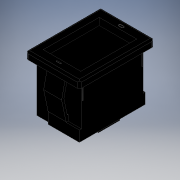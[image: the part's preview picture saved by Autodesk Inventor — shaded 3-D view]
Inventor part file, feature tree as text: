
AUTODESK INVENTOR PART (.ipt)
format: ipt  version: 2019 (Build 230136000, 136)  size: 359,936 bytes
history: native  units: in
note: dims shown in document units (in); Inventor stores cm internally (conversion verified against a paired STEP export)
features: other x21, extrude x11, sketch x11
ambient origin geometry x8: Origin, YZ Plane, XZ Plane, XY Plane, X Axis, Y Axis, Z Axis, Center Point
bodies: Solid1 (feature_tree)
feature tree (43):
  extrude  "Extrusion1"  Depth=0.079in TaperAngle=0.0deg
  extrude  "Extrusion2"  Depth=0.598in TaperAngle=0.0deg
  extrude  "Extrusion3"  Depth=0.2in TaperAngle=0.0deg
  extrude  "Extrusion4"  Depth=0.082in TaperAngle=0.0deg
  extrude  "Extrusion5"  Depth=0.039in TaperAngle=0.0deg
  extrude  "Extrusion6"  TaperAngle=0.0deg  [1 undecoded]
  extrude  "Extrusion7"  [1 undecoded]
  extrude  "Extrusion8"  [1 undecoded]
  extrude  "Extrusion9"  [1 undecoded]
  extrude  "Extrusion10"  [1 undecoded]
  extrude  "Extrusion11"  [1 undecoded]
  other  "to_dummy_XY"
  other  "to_dummy_YZ"
  other  "to_dummy_ZX"
  other  "to_dummy_X"
  other  "to_dummy_Y"
  other  "to_dummy_Z"
  other  "to_dummy_Center"
  other  "to_rocker_XY"
  other  "to_rocker_YZ"
  other  "to_rocker_ZX"
  other  "to_rocker_X"
  other  "to_rocker_Y"
  other  "to_rocker_Z"
  other  "to_rocker_Center"
  other  "to_terminals_XY"
  other  "to_terminals_YZ"
  other  "to_terminals_ZX"
  other  "to_terminals_X"
  other  "to_terminals_Y"
  other  "to_terminals_Z"
  other  "to_terminals_Center"
  sketch  "Sketch_7"  dims[d20=0.245in d21=0.0in d22=0.0in d23=0.0in]
  sketch  "Sketch_8"
  sketch  "Sketch_9"
  sketch  "Sketch_6"  dims[d16=0.082in d17=0.0in d18=0.039in d19=0.0in]
  sketch  "Sketch_1"  dims[d0=0.079in d1=0.0in d2=1.2in d3=0.0in]
  sketch  "Sketch_10"
  sketch  "Sketch_13"
  sketch  "Sketch_2"  dims[d4=1.2in d5=0.0in d6=0.598in d7=0.0in]
  sketch  "Sketch_3"  dims[d8=0.119in d9=0.0in d10=0.2in d11=0.0in]
  sketch  "Sketch_12"
  sketch  "Sketch_4"  dims[d12=1.0in d13=0.0in d14=0.082in d15=0.0in]
note: 6 required parameter values undecoded (feature->parameter linkage not recoverable at this tier; creation-order binding heuristic only, values carry confidence <= 0.55)
